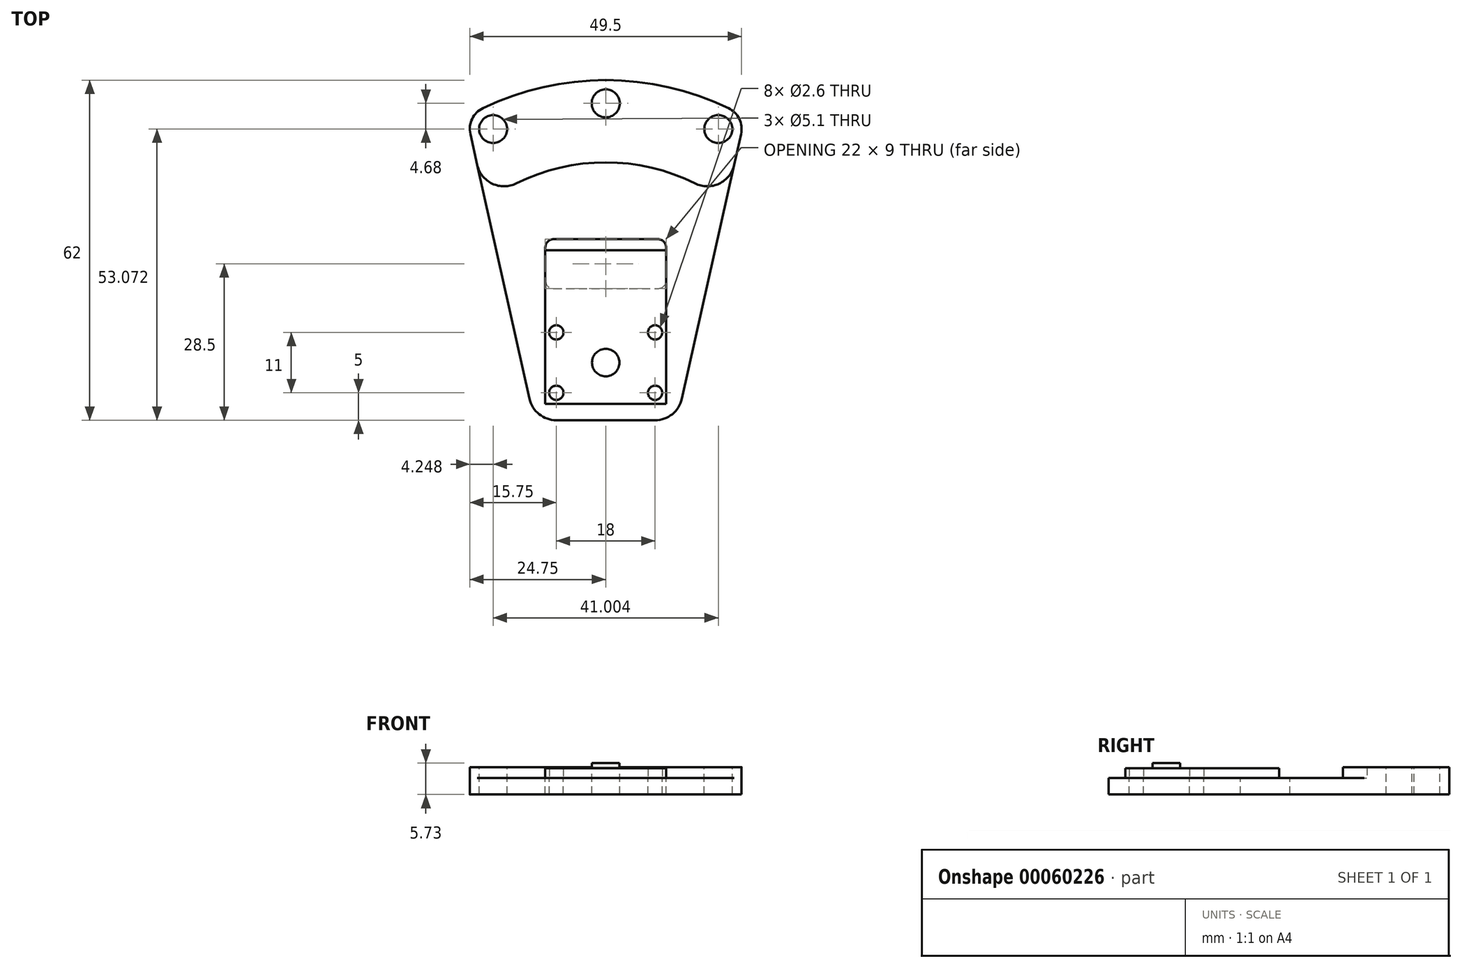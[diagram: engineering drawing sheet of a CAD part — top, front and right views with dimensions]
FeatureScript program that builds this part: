
annotation { "Feature Type Name" : "Feature", "Feature Type Description" : "" }
export const myFeature = defineFeature(function(context is Context, id is Id, definition is map)
    precondition{}
    {
        {
            var Q0;
            Q0=qCreatedBy(makeId("Top.planeOp"),FACE);
            var sketch = newSketch(context, id + "F0", { "sketchPlane" : qUnion([Q0])});
            skLineSegment(sketch, "E0.bottom", {"start": v(-11, 20.5) * mm, "end": v(11, 20.5) * mm});
            skLineSegment(sketch, "E0.top", {"start": v(-11, -7.5) * mm, "end": v(11, -7.5) * mm});
            skLineSegment(sketch, "E0.left", {"start": v(-11, 20.5) * mm, "end": v(-11, -7.5) * mm});
            skLineSegment(sketch, "E0.right", {"start": v(11, 20.5) * mm, "end": v(11, -7.5) * mm});
            skPoint(sketch, "E1", {"position": v(0, 0) * mm});
            skPoint(sketch, "E1.positionSnap0", {"position": v(0, -7.5) * mm});
            skLineSegment(sketch, "E2.rect.bottom", {"start": v(9, 5.5) * mm, "end": v(-9, 5.5) * mm, "construction": true});
            skLineSegment(sketch, "E2.rect.top", {"start": v(9, -5.5) * mm, "end": v(-9, -5.5) * mm, "construction": true});
            skLineSegment(sketch, "E2.rect.left", {"start": v(9, 5.5) * mm, "end": v(9, -5.5) * mm, "construction": true});
            skLineSegment(sketch, "E2.rect.right", {"start": v(-9, 5.5) * mm, "end": v(-9, -5.5) * mm, "construction": true});
            skCircle(sketch, "E3", {"center": v(-9, 5.5) * mm, "radius": 1.3 * mm});
            skCircle(sketch, "E4", {"center": v(9, 5.5) * mm, "radius": 1.3 * mm});
            skCircle(sketch, "E5", {"center": v(9, -5.5) * mm, "radius": 1.3 * mm});
            skCircle(sketch, "E6", {"center": v(-9, -5.5) * mm, "radius": 1.3 * mm});
            skLineSegment(sketch, "E7", {"start": v(9, -5.5) * mm, "end": v(9, -7.5) * mm, "construction": true});
            skLineSegment(sketch, "E8", {"start": v(9, -5.5) * mm, "end": v(11, -5.5) * mm, "construction": true});
            skLineSegment(sketch, "E9.rect.bottom", {"start": v(2.5, 2.5) * mm, "end": v(-2.5, 2.5) * mm, "construction": true});
            skLineSegment(sketch, "E9.rect.top", {"start": v(2.5, -2.5) * mm, "end": v(-2.5, -2.5) * mm, "construction": true});
            skLineSegment(sketch, "E9.rect.left", {"start": v(2.5, 2.5) * mm, "end": v(2.5, -2.5) * mm, "construction": true});
            skLineSegment(sketch, "E9.rect.right", {"start": v(-2.5, 2.5) * mm, "end": v(-2.5, -2.5) * mm, "construction": true});
            skCircle(sketch, "E10", {"center": v(0, 0) * mm, "radius": 2.5 * mm});
            skSolve(sketch);
        }
        {
            var Q0;
            Q0 = qSketchRegion(id + "F0", true);
            var Q1;
            Q1=makeQuery(id+"F0.imprint","IMPRINT",FACE,{"disambiguationData":[TD([[makeQuery(id+"F0.imprint","IMPRINT",EDGE,{"derivedFrom":sQuery(id+"F0.wireOp",EDGE,"E9.rect.bottom")}),1.0]])]});
            extrude(context, id + "F1", {"entities" : qUnion([Q0, Q1]), "depth" : 1.8 * mm});
        }
        {
            var Q0;
            Q0=makeQuery(id+"F1.opExtrude","CAP_FACE",FACE,{"disambiguationData":[OSD([sQuery(id+"F0.wireOp",EDGE,"E0.bottom"),sQuery(id+"F0.wireOp",EDGE,"E0.top"),sQuery(id+"F0.wireOp",EDGE,"E0.left"),sQuery(id+"F0.wireOp",EDGE,"E0.right"),sQuery(id+"F0.wireOp",EDGE,"E3"),sQuery(id+"F0.wireOp",EDGE,"E4"),sQuery(id+"F0.wireOp",EDGE,"E5"),sQuery(id+"F0.wireOp",EDGE,"E6"),sQuery(id+"F0.wireOp",EDGE,"E10")])],"isStart":true});
            var sketch = newSketch(context, id + "F2", { "sketchPlane" : qUnion([Q0])});
            skCircle(sketch, "E11", {"center": v(0, 0) * mm, "radius": 2.5 * mm});
            skSolve(sketch);
        }
        {
            var Q0;
            Q0 = qSketchRegion(id + "F2", true);
            extrude(context, id + "F3", {"entities" : qUnion([Q0]), "operationType" : NewBodyOperationType.ADD, "oppositeDirection" : true, "depth" : 2.73 * mm});
        }
        {
            var Q0;
            Q0=makeQuery(id+"F3.boolean.opBoolean","MERGE",FACE,{"derivedFrom":[makeQuery(id+"F1.opExtrude","CAP_FACE",FACE,{"disambiguationData":[OSD([sQuery(id+"F0.wireOp",EDGE,"E0.bottom"),sQuery(id+"F0.wireOp",EDGE,"E0.top"),sQuery(id+"F0.wireOp",EDGE,"E0.left"),sQuery(id+"F0.wireOp",EDGE,"E0.right"),sQuery(id+"F0.wireOp",EDGE,"E3"),sQuery(id+"F0.wireOp",EDGE,"E4"),sQuery(id+"F0.wireOp",EDGE,"E5"),sQuery(id+"F0.wireOp",EDGE,"E6"),sQuery(id+"F0.wireOp",EDGE,"E10")])],"isStart":true}),makeQuery(id+"F3.opExtrude","CAP_FACE",FACE,{"disambiguationData":[OSD([sQuery(id+"F2.wireOp",EDGE,"E11")])],"isStart":true})]});
            var sketch = newSketch(context, id + "F4", { "sketchPlane" : qUnion([Q0])});
            skLineSegment(sketch, "E12", {"start": v(-9, 10.5) * mm, "end": v(9, 10.5) * mm});
            skCircle(sketch, "E13", {"center": v(-20.5, -42.57) * mm, "radius": 2.55 * mm});
            skCircle(sketch, "E14", {"center": v(20.5, -42.57) * mm, "radius": 2.55 * mm});
            skArc(sketch, "E15", {"start": v(-20.5, -42.57) * mm, "mid": v(0, -47.25) * mm, "end": v(20.5, -42.57) * mm, "construction": true});
            skPoint(sketch, "E16", {"position": v(0, -47.25) * mm});
            skCircle(sketch, "E17", {"center": v(0, -47.25) * mm, "radius": 2.55 * mm});
            skLineSegment(sketch, "E18", {"start": v(13.88, 6.59) * mm, "end": v(24.65, -41.65) * mm});
            skLineSegment(sketch, "E19", {"start": v(-13.88, 6.59) * mm, "end": v(-24.65, -41.65) * mm});
            skArc(sketch, "E20", {"start": v(-22.35, -46.4) * mm, "mid": v(0, -51.5) * mm, "end": v(22.35, -46.4) * mm});
            skPoint(sketch, "E21", {"position": v(0, -51.5) * mm});
            skPoint(sketch, "E22.visualSharp", {"position": v(-25.36, -44.82) * mm});
            skArc(sketch, "E22.filletArc", {"start": v(-24.65, -41.65) * mm, "mid": v(-24.32, -44.42) * mm, "end": v(-22.35, -46.4) * mm});
            skPoint(sketch, "E23.visualSharp", {"position": v(25.36, -44.82) * mm});
            skArc(sketch, "E23.filletArc", {"start": v(22.35, -46.4) * mm, "mid": v(24.32, -44.42) * mm, "end": v(24.65, -41.65) * mm});
            skCircle(sketch, "E24", {"center": v(-9, -5.5) * mm, "radius": 1.3 * mm});
            skCircle(sketch, "E25", {"center": v(9, 5.5) * mm, "radius": 1.3 * mm});
            skCircle(sketch, "E26", {"center": v(9, -5.5) * mm, "radius": 1.3 * mm});
            skCircle(sketch, "E27", {"center": v(-9, 5.5) * mm, "radius": 1.3 * mm});
            skLineSegment(sketch, "E28.bottom", {"start": v(-11, -13.5) * mm, "end": v(11, -13.5) * mm});
            skLineSegment(sketch, "E28.top", {"start": v(-11, -22.5) * mm, "end": v(11, -22.5) * mm});
            skLineSegment(sketch, "E28.left", {"start": v(-11, -13.5) * mm, "end": v(-11, -22.5) * mm});
            skLineSegment(sketch, "E28.right", {"start": v(11, -13.5) * mm, "end": v(11, -22.5) * mm});
            skPoint(sketch, "E29.visualSharp", {"position": v(-13, 10.5) * mm});
            skArc(sketch, "E29.filletArc", {"start": v(-9, 10.5) * mm, "mid": v(-12.13, 9.4) * mm, "end": v(-13.88, 6.59) * mm});
            skPoint(sketch, "E30.visualSharp", {"position": v(13, 10.5) * mm});
            skArc(sketch, "E30.filletArc", {"start": v(13.88, 6.59) * mm, "mid": v(12.13, 9.4) * mm, "end": v(9, 10.5) * mm});
            skArc(sketch, "E31", {"start": v(-21.87, -29.22) * mm, "mid": v(0, -36.5) * mm, "end": v(21.87, -29.22) * mm});
            skSolve(sketch);
        }
        {
            var Q0;
            Q0=makeQuery(id+"F4.imprint","IMPRINT",FACE,{"disambiguationData":[TD([[makeQuery(id+"F4.imprint","IMPRINT",EDGE,{"derivedFrom":sQuery(id+"F4.wireOp",EDGE,"E24")}),1.0]])]});
            var Q1;
            Q1=makeQuery(id+"F4.imprint","IMPRINT",FACE,{"disambiguationData":[TD([[makeQuery(id+"F4.imprint","IMPRINT",EDGE,{"derivedFrom":sQuery(id+"F4.wireOp",EDGE,"E12")}),-1.0]])]});
            var Q2;
            Q2=makeQuery(id+"F4.imprint","IMPRINT",FACE,{"disambiguationData":[TD([[makeQuery(id+"F4.imprint","IMPRINT",EDGE,{"derivedFrom":sQuery(id+"F4.wireOp",EDGE,"E13")}),-1.0]])]});
            extrude(context, id + "F5", {"entities" : qUnion([Q0, Q1, Q2]), "depth" : 3 * mm});
        }
        {
            var Q0;
            Q0=makeQuery(id+"F4.imprint","IMPRINT",FACE,{"disambiguationData":[TD([[makeQuery(id+"F4.imprint","IMPRINT",EDGE,{"derivedFrom":sQuery(id+"F4.wireOp",EDGE,"E13")}),-1.0]])]});
            extrude(context, id + "F6", {"entities" : qUnion([Q0]), "operationType" : NewBodyOperationType.ADD, "oppositeDirection" : true, "depth" : 2 * mm});
        }
        {
            var Q0;
            Q0=makeQuery(id+"F6.opExtrude","SWEPT_EDGE",EDGE,{"disambiguationData":[OSD([sQuery(id+"F4.wireOp",EDGE,"E18"),sQuery(id+"F4.wireOp",EDGE,"E31")])]});
            var Q1;
            Q1=makeQuery(id+"F6.opExtrude","SWEPT_EDGE",EDGE,{"disambiguationData":[OSD([sQuery(id+"F4.wireOp",EDGE,"E19"),sQuery(id+"F4.wireOp",EDGE,"E31")])]});
            fillet(context, id + "F7", {"entities" : qUnion([Q0, Q1]), "radius" : 5 * mm, "tangentPropagation" : true, "allowEdgeOverflow" : false});
        }
        {
            var Q0;
            Q0=makeQuery(id+"F5.opExtrude","SWEPT_EDGE",EDGE,{"disambiguationData":[OSD([sQuery(id+"F4.wireOp",EDGE,"E28.top"),sQuery(id+"F4.wireOp",EDGE,"E28.right")])]});
            var Q1;
            Q1=makeQuery(id+"F5.opExtrude","SWEPT_EDGE",EDGE,{"disambiguationData":[OSD([sQuery(id+"F0.wireOp",EDGE,"E0.right"),sQuery(id+"F4.wireOp",EDGE,"E28.bottom"),sQuery(id+"F4.wireOp",EDGE,"E28.right")])]});
            var Q2;
            Q2=makeQuery(id+"F5.opExtrude","SWEPT_EDGE",EDGE,{"disambiguationData":[OSD([sQuery(id+"F4.wireOp",EDGE,"E28.top"),sQuery(id+"F4.wireOp",EDGE,"E28.left")])]});
            var Q3;
            Q3=makeQuery(id+"F5.opExtrude","SWEPT_EDGE",EDGE,{"disambiguationData":[OSD([sQuery(id+"F0.wireOp",EDGE,"E0.left"),sQuery(id+"F4.wireOp",EDGE,"E28.bottom"),sQuery(id+"F4.wireOp",EDGE,"E28.left")])]});
            fillet(context, id + "F8", {"entities" : qUnion([Q0, Q1, Q2, Q3]), "radius" : 1.5 * mm, "tangentPropagation" : true, "allowEdgeOverflow" : false});
        }
    });
